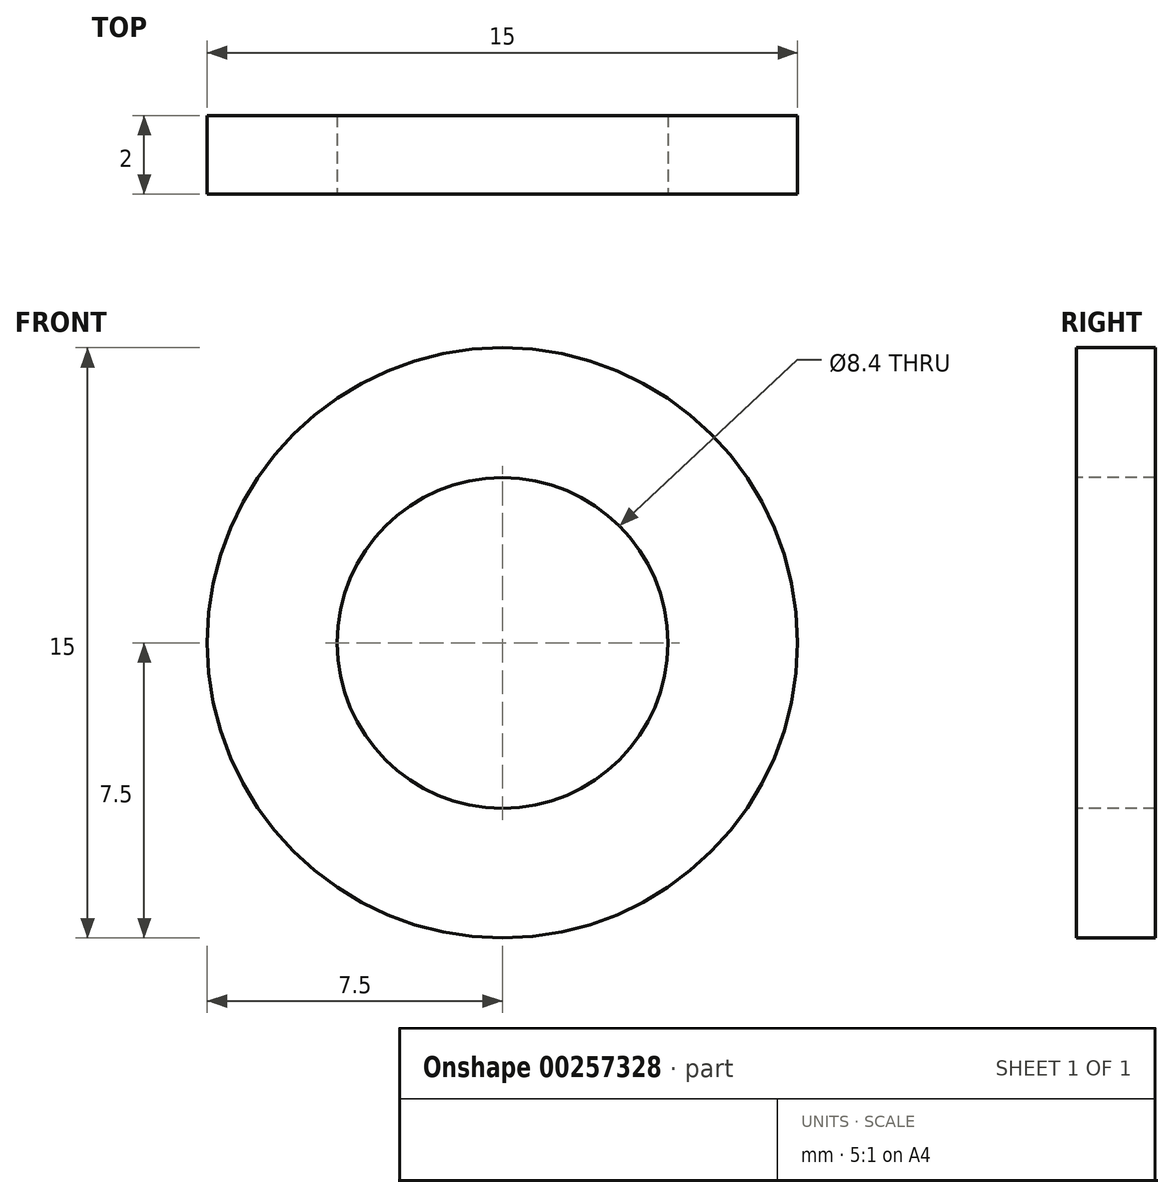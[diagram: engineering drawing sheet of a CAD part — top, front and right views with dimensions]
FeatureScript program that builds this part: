
annotation { "Feature Type Name" : "Feature", "Feature Type Description" : "" }
export const myFeature = defineFeature(function(context is Context, id is Id, definition is map)
    precondition{}
    {
        {
            var Q0;
            Q0=qCreatedBy(makeId("Front.planeOp"),FACE);
            var sketch = newSketch(context, id + "F0", { "sketchPlane" : qUnion([Q0])});
            skCircle(sketch, "E0", {"center": v(0, 0) * mm, "radius": 7.5 * mm});
            skSolve(sketch);
        }
        {
            var Q0;
            Q0=makeQuery(id+"F0.imprint","IMPRINT",FACE,{"disambiguationData":[TD([[makeQuery(id+"F0.imprint","IMPRINT",EDGE,{"derivedFrom":sQuery(id+"F0.wireOp",EDGE,"E0")}),1.0]])]});
            extrude(context, id + "F1", {"entities" : qUnion([Q0]), "oppositeDirection" : true, "depth" : 2 * mm});
        }
        {
            var Q0;
            Q0=sQuery(id+"F0.wireOp",VERTEX,"E0.center");
            var Q1;
            Q1=makeQuery(id+"F1.opExtrude","SWEPT_BODY",BODY,{"disambiguationData":[OSD([sQuery(id+"F0.wireOp",EDGE,"E0")])]});
            hole(context, id + "F2", {"style" : HoleStyle.SIMPLE, "endStyle" : HoleEndStyle.THROUGH, "standardTappedOrClearance" : lookupTablePath({ "standard" : "Custom", "fit" : "Normal", "engagement" : "75%", "pitch" : "1 mm", "size" : "M8", "type" : "Tapped" }), "standardBlindInLast" : lookupTablePath({ "fit" : "Standard", "standard" : "Custom", "engagement" : "75%", "pitch" : "1 mm", "size" : "M8", "type" : "Tapped" }), "holeDiameter" : 8.4 * mm, "showTappedDepth" : true, "tappedDepth" : 12 * mm, "tapClearance" : 3, "locations" : qUnion([Q0]), "scope" : qUnion([Q1])});
        }
    });
